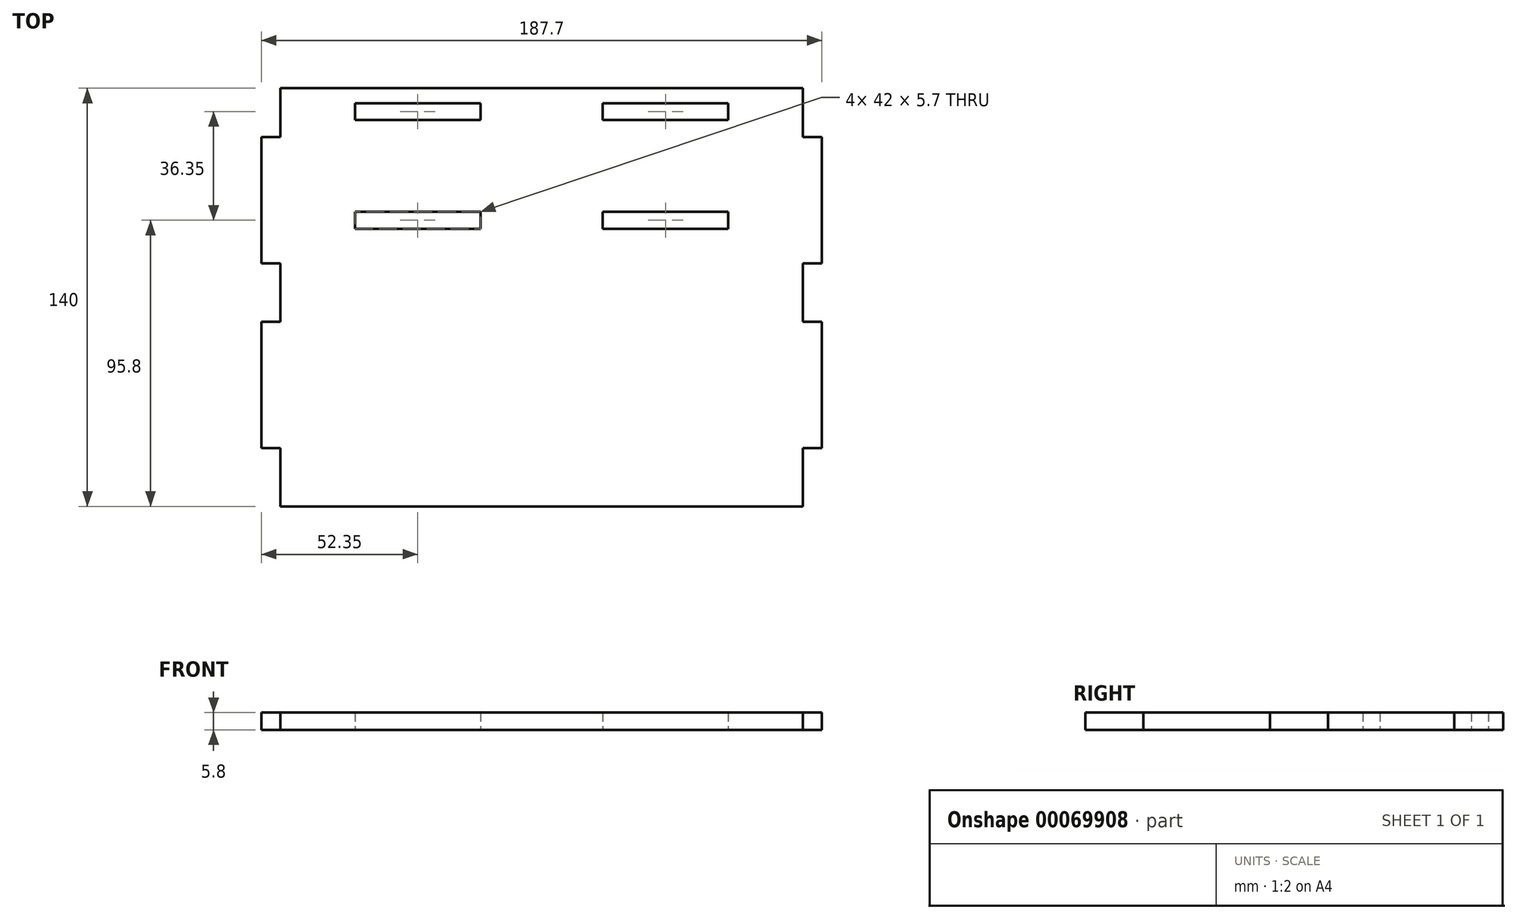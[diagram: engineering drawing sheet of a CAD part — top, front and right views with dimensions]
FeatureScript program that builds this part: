
annotation { "Feature Type Name" : "Feature", "Feature Type Description" : "" }
export const myFeature = defineFeature(function(context is Context, id is Id, definition is map)
    precondition{}
    {
        {
            var Q0;
            Q0=qCreatedBy(makeId("Top.planeOp"),FACE);
            var sketch = newSketch(context, id + "F0", { "sketchPlane" : qUnion([Q0])});
            skLineSegment(sketch, "E0.bottom", {"start": v(87.5, 70) * mm, "end": v(-87.5, 70) * mm});
            skLineSegment(sketch, "E0.top", {"start": v(87.5, -70) * mm, "end": v(-87.5, -70) * mm});
            skLineSegment(sketch, "E0.left", {"start": v(87.5, 70) * mm, "end": v(87.5, 53.65) * mm});
            skLineSegment(sketch, "E0.right", {"start": v(-87.5, 70) * mm, "end": v(-87.5, 53.65) * mm});
            skPoint(sketch, "E0.middle", {"position": v(0, 0) * mm});
            skLineSegment(sketch, "E1.bottom", {"start": v(87.5, 53.65) * mm, "end": v(93.85, 53.65) * mm});
            skLineSegment(sketch, "E1.top", {"start": v(87.5, 11.35) * mm, "end": v(93.85, 11.35) * mm});
            skLineSegment(sketch, "E1.right", {"start": v(93.85, 53.65) * mm, "end": v(93.85, 11.35) * mm});
            skLineSegment(sketch, "E2.trimOffspring", {"start": v(87.5, 11.35) * mm, "end": v(87.5, -8.17) * mm});
            skLineSegment(sketch, "E3.bottom", {"start": v(87.5, -50.48) * mm, "end": v(93.85, -50.48) * mm});
            skLineSegment(sketch, "E3.top", {"start": v(87.5, -8.17) * mm, "end": v(93.85, -8.17) * mm});
            skLineSegment(sketch, "E3.right", {"start": v(93.85, -50.48) * mm, "end": v(93.85, -8.17) * mm});
            skLineSegment(sketch, "E4.trimOffspring", {"start": v(87.5, -50.48) * mm, "end": v(87.5, -70) * mm});
            skPoint(sketch, "E5", {"position": v(0, 70) * mm});
            skPoint(sketch, "E6", {"position": v(0, -70) * mm});
            skLineSegment(sketch, "E7.bottom", {"start": v(-87.5, 53.65) * mm, "end": v(-93.85, 53.65) * mm});
            skLineSegment(sketch, "E7.top", {"start": v(-87.5, 11.35) * mm, "end": v(-93.85, 11.35) * mm});
            skLineSegment(sketch, "E7.right", {"start": v(-93.85, 53.65) * mm, "end": v(-93.85, 11.35) * mm});
            skLineSegment(sketch, "E8.bottom", {"start": v(-87.5, -8.17) * mm, "end": v(-93.85, -8.17) * mm});
            skLineSegment(sketch, "E8.top", {"start": v(-87.5, -50.48) * mm, "end": v(-93.85, -50.48) * mm});
            skLineSegment(sketch, "E8.right", {"start": v(-93.85, -8.17) * mm, "end": v(-93.85, -50.48) * mm});
            skLineSegment(sketch, "E9.trimOffspring", {"start": v(-87.5, 11.35) * mm, "end": v(-87.5, -8.17) * mm});
            skLineSegment(sketch, "E10.trimOffspring", {"start": v(-87.5, -50.48) * mm, "end": v(-87.5, -70) * mm});
            skLineSegment(sketch, "E11.bottom", {"start": v(-62.5, 65) * mm, "end": v(-20.5, 65) * mm});
            skLineSegment(sketch, "E11.top", {"start": v(-62.5, 59.3) * mm, "end": v(-20.5, 59.3) * mm});
            skLineSegment(sketch, "E11.left", {"start": v(-62.5, 65) * mm, "end": v(-62.5, 59.3) * mm});
            skLineSegment(sketch, "E11.right", {"start": v(-20.5, 65) * mm, "end": v(-20.5, 59.3) * mm});
            skLineSegment(sketch, "E12.bottom", {"start": v(20.5, 65) * mm, "end": v(62.5, 65) * mm});
            skLineSegment(sketch, "E12.top", {"start": v(20.5, 59.3) * mm, "end": v(62.5, 59.3) * mm});
            skLineSegment(sketch, "E12.left", {"start": v(20.5, 65) * mm, "end": v(20.5, 59.3) * mm});
            skLineSegment(sketch, "E12.right", {"start": v(62.5, 65) * mm, "end": v(62.5, 59.3) * mm});
            skLineSegment(sketch, "E13.bottom", {"start": v(-62.5, 28.65) * mm, "end": v(-20.5, 28.65) * mm});
            skLineSegment(sketch, "E13.top", {"start": v(-62.5, 22.95) * mm, "end": v(-20.5, 22.95) * mm});
            skLineSegment(sketch, "E13.left", {"start": v(-62.5, 28.65) * mm, "end": v(-62.5, 22.95) * mm});
            skLineSegment(sketch, "E13.right", {"start": v(-20.5, 28.65) * mm, "end": v(-20.5, 22.95) * mm});
            skLineSegment(sketch, "E14.bottom", {"start": v(20.5, 28.65) * mm, "end": v(62.5, 28.65) * mm});
            skLineSegment(sketch, "E14.top", {"start": v(20.5, 22.95) * mm, "end": v(62.5, 22.95) * mm});
            skLineSegment(sketch, "E14.left", {"start": v(20.5, 28.65) * mm, "end": v(20.5, 22.95) * mm});
            skLineSegment(sketch, "E14.right", {"start": v(62.5, 28.65) * mm, "end": v(62.5, 22.95) * mm});
            skSolve(sketch);
        }
        {
            var Q0;
            Q0=makeQuery(id+"F0.imprint","IMPRINT",FACE,{"disambiguationData":[TD([[makeQuery(id+"F0.imprint","IMPRINT",EDGE,{"derivedFrom":sQuery(id+"F0.wireOp",EDGE,"E0.bottom")}),1.0]])]});
            extrude(context, id + "F1", {"entities" : qUnion([Q0]), "depth" : 5.8 * mm});
        }
    });
